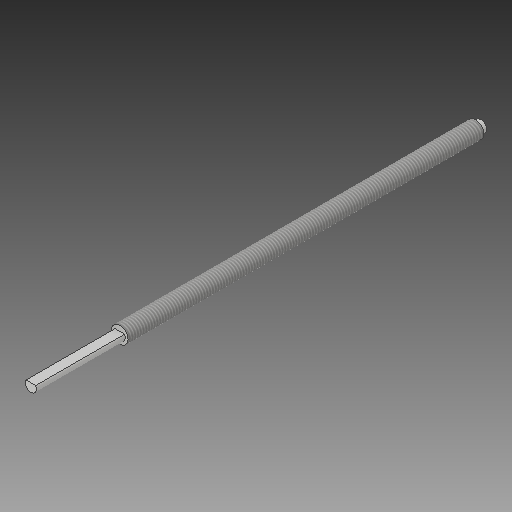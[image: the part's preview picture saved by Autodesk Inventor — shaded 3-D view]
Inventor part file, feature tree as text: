
AUTODESK INVENTOR PART (.ipt)
format: ipt  version: 2019 (Build 230136000, 136)  size: 108,544 bytes
history: native  units: in
note: dims shown in document units (in); Inventor stores cm internally (conversion verified against a paired STEP export)
features: extrude x3, sketch x3, thread x1
ambient origin geometry x8: Origin, YZ Plane, XZ Plane, XY Plane, X Axis, Y Axis, Z Axis, Center Point
bodies: Solid1 (feature_tree)
feature tree (7):
  extrude  "Extrusion1"  Depth=10.0in TaperAngle=0.0deg
  thread  "Thread1"  [1 undecoded]
  extrude  "Extrusion2"  Depth=0.0625in
  extrude  "Extrusion3"  Depth=0.125in
  sketch  "Sketch1"  dims[d0=0.375in d1=10.0in d2=0.0in d3=1.0in d4=0.0in]
  sketch  "Sketch2"  dims[d5=0.25in d6=0.0625in]
  sketch  "Sketch4"  dims[d7=2.0in d8=0.0in d16=0.25in d17=0.125in d18=0.0in]
note: 1 required parameter value undecoded (feature->parameter linkage not recoverable at this tier; creation-order binding heuristic only, values carry confidence <= 0.55)
